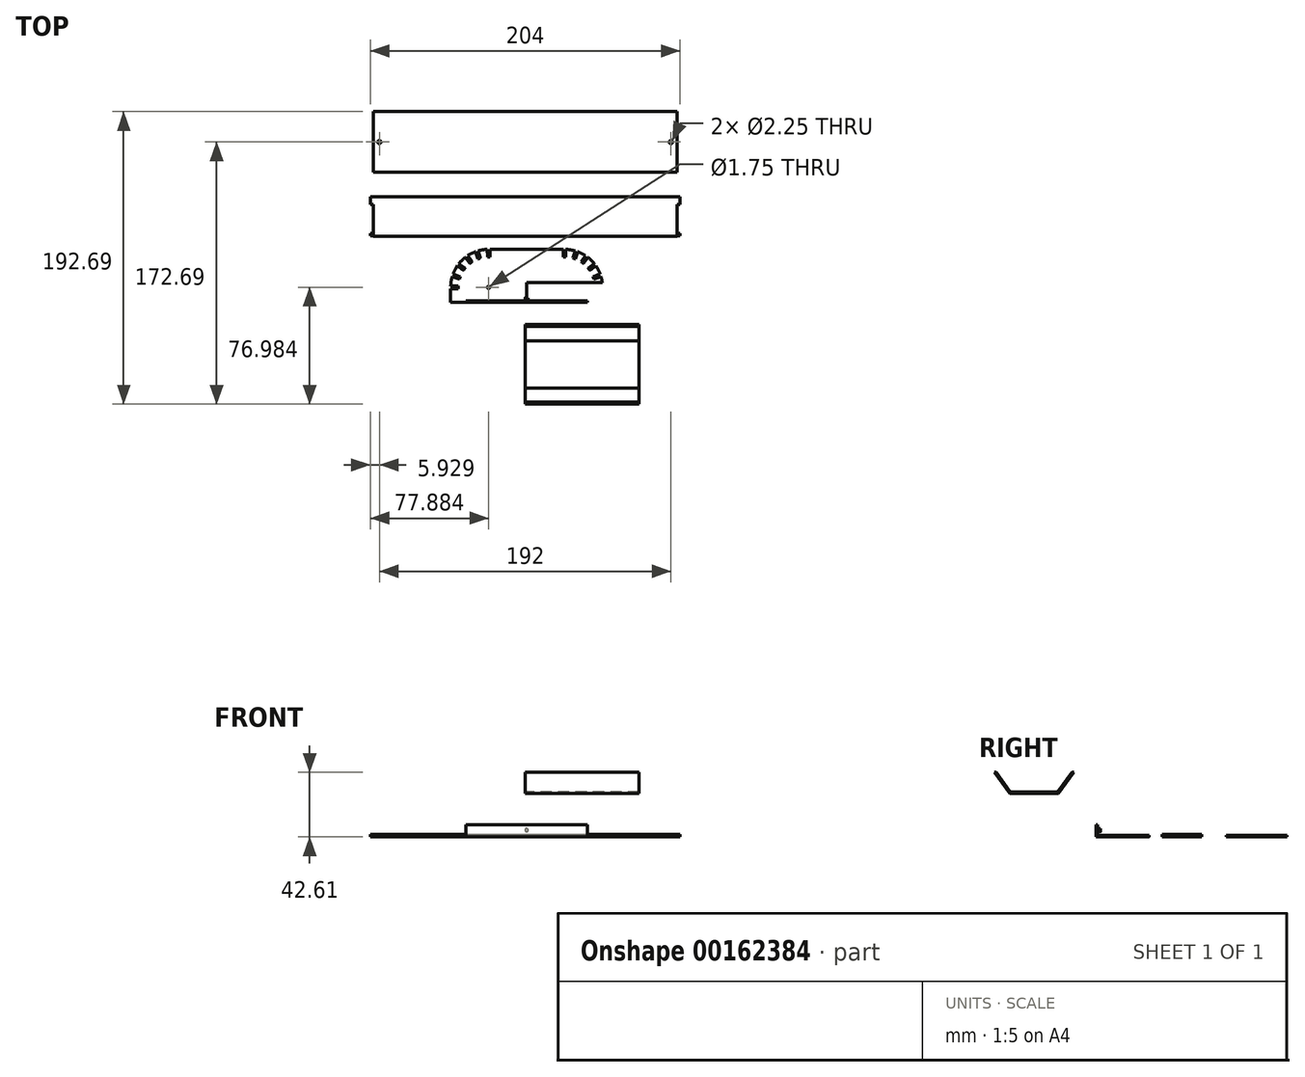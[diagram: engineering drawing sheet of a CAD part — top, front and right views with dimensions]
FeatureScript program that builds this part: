
annotation { "Feature Type Name" : "Feature", "Feature Type Description" : "" }
export const myFeature = defineFeature(function(context is Context, id is Id, definition is map)
    precondition{}
    {
        {
            var Q0;
            Q0=qCreatedBy(makeId("Top.planeOp"),FACE);
            var sketch = newSketch(context, id + "F0", { "sketchPlane" : qUnion([Q0])});
            skLineSegment(sketch, "E0.bottom", {"start": v(0, 0) * mm, "end": v(100, 0) * mm});
            skLineSegment(sketch, "E0.left", {"start": v(0, 0) * mm, "end": v(0, 26) * mm});
            skLineSegment(sketch, "E0.right", {"start": v(100, 0) * mm, "end": v(100, 21) * mm});
            skLineSegment(sketch, "E1", {"start": v(102, 26) * mm, "end": v(102, 21) * mm});
            skLineSegment(sketch, "E2", {"start": v(0, 26) * mm, "end": v(102, 26) * mm});
            skLineSegment(sketch, "E3", {"start": v(100, 21) * mm, "end": v(102, 21) * mm});
            skLineSegment(sketch, "E4.MirrorCS", {"start": v(-102, 26) * mm, "end": v(-102, 21) * mm});
            skLineSegment(sketch, "E5.MirrorCS", {"start": v(0, 26) * mm, "end": v(-102, 26) * mm});
            skLineSegment(sketch, "E6.MirrorCS", {"start": v(0, 0) * mm, "end": v(-100, 0) * mm});
            skLineSegment(sketch, "E7.MirrorCS", {"start": v(-100, 0) * mm, "end": v(-100, 21) * mm});
            skLineSegment(sketch, "E8.MirrorCS", {"start": v(-100, 21) * mm, "end": v(-102, 21) * mm});
            skPoint(sketch, "E9", {"position": v(0, 21) * mm});
            skPoint(sketch, "E10", {"position": v(0, 1) * mm});
            skSolve(sketch);
        }
        {
            var Q0;
            Q0=qCreatedBy(makeId("Top.planeOp"),FACE);
            var sketch = newSketch(context, id + "F1", { "sketchPlane" : qUnion([Q0])});
            skLineSegment(sketch, "E11", {"start": v(0.88, -33.7) * mm, "end": v(0.88, -8.7) * mm});
            skLineSegment(sketch, "E12", {"start": v(0.88, -8.7) * mm, "end": v(25, -8.7) * mm});
            skLineSegment(sketch, "E13", {"start": v(25.88, -30.7) * mm, "end": v(25.88, -30.87) * mm});
            skLineSegment(sketch, "E14", {"start": v(11.63, -33.7) * mm, "end": v(0.88, -33.7) * mm});
            skArc(sketch, "E15", {"start": v(26.76, -8.72) * mm, "mid": v(29.85, -9.02) * mm, "end": v(32.87, -9.7) * mm});
            skLineSegment(sketch, "E16.2", {"start": v(50.88, -43.7) * mm, "end": v(0.88, -43.7) * mm});
            skLineSegment(sketch, "E17.1", {"start": v(25.88, -30.7) * mm, "end": v(0.88, -30.7) * mm});
            skLineSegment(sketch, "E17.2", {"start": v(50.7, -30.7) * mm, "end": v(25.88, -30.7) * mm});
            skLineSegment(sketch, "E18", {"start": v(50.88, -34.58) * mm, "end": v(50.88, -43.7) * mm});
            skCircle(sketch, "E19", {"center": v(25.88, -33.7) * mm, "radius": 0.88 * mm});
            skLineSegment(sketch, "E20.0", {"start": v(45.14, -28.29) * mm, "end": v(49.87, -26.66) * mm});
            skLineSegment(sketch, "E21.0", {"start": v(31.3, -14.45) * mm, "end": v(32.87, -9.7) * mm});
            skArc(sketch, "E22.trimOffspring", {"start": v(34.53, -10.25) * mm, "mid": v(37.2, -11.42) * mm, "end": v(39.73, -12.89) * mm});
            skArc(sketch, "E23.trimOffspring", {"start": v(41.15, -13.9) * mm, "mid": v(43.45, -15.92) * mm, "end": v(45.48, -18.19) * mm});
            skArc(sketch, "E24.trimOffspring", {"start": v(46.52, -19.6) * mm, "mid": v(48.09, -22.21) * mm, "end": v(49.32, -25) * mm});
            skArc(sketch, "E25.trimOffspring", {"start": v(49.87, -26.66) * mm, "mid": v(50.56, -29.72) * mm, "end": v(50.87, -32.83) * mm});
            skLineSegment(sketch, "E26", {"start": v(0.88, -43.7) * mm, "end": v(0.88, -33.7) * mm});
            skLineSegment(sketch, "E27.MirrorCS", {"start": v(0.88, -43.7) * mm, "end": v(10.88, -43.7) * mm});
            skLineSegment(sketch, "E28.MirrorCS", {"start": v(26.68, -13.7) * mm, "end": v(24.93, -13.7) * mm});
            skLineSegment(sketch, "E29.MirrorCS", {"start": v(0.88, -30.7) * mm, "end": v(20.88, -30.7) * mm});
            skLineSegment(sketch, "E30.trimOffspring", {"start": v(24.93, -13.7) * mm, "end": v(25.88, -13.7) * mm});
            skArc(sketch, "E31.trimOffspring", {"start": v(31.3, -14.45) * mm, "mid": v(32.14, -14.7) * mm, "end": v(32.96, -15) * mm});
            skArc(sketch, "E32.trimOffspring", {"start": v(36.85, -16.98) * mm, "mid": v(37.57, -17.48) * mm, "end": v(38.27, -18) * mm});
            skArc(sketch, "E33.trimOffspring", {"start": v(41.48, -21.2) * mm, "mid": v(42.02, -21.89) * mm, "end": v(42.52, -22.6) * mm});
            skArc(sketch, "E34.trimOffspring", {"start": v(44.59, -26.62) * mm, "mid": v(44.88, -27.45) * mm, "end": v(45.14, -28.29) * mm});
            skLineSegment(sketch, "E35.trimOffspring", {"start": v(24.93, -13.7) * mm, "end": v(25, -8.7) * mm});
            skLineSegment(sketch, "E36.trimOffspring", {"start": v(26.68, -13.7) * mm, "end": v(26.76, -8.72) * mm});
            skPoint(sketch, "E37.start.orphan", {"position": v(25, -33.7) * mm});
            skLineSegment(sketch, "E38.trimOffspring", {"start": v(36.85, -16.98) * mm, "end": v(39.73, -12.89) * mm});
            skLineSegment(sketch, "E39.trimOffspring", {"start": v(38.27, -18) * mm, "end": v(41.15, -13.9) * mm});
            skLineSegment(sketch, "E40.trimOffspring", {"start": v(44.59, -26.62) * mm, "end": v(49.32, -25) * mm});
            skLineSegment(sketch, "E41.trimOffspring", {"start": v(42.52, -22.6) * mm, "end": v(46.52, -19.6) * mm});
            skLineSegment(sketch, "E42.trimOffspring", {"start": v(41.48, -21.2) * mm, "end": v(45.48, -18.19) * mm});
            skLineSegment(sketch, "E43.trimOffspring", {"start": v(32.96, -15) * mm, "end": v(34.53, -10.25) * mm});
            skPoint(sketch, "E44.start.orphan", {"position": v(26.76, -33.7) * mm});
            skLineSegment(sketch, "E45.MirrorCS", {"start": v(-9.87, -33.7) * mm, "end": v(0.88, -33.7) * mm});
            skLineSegment(sketch, "E46.0", {"start": v(50.88, -32.83) * mm, "end": v(45.88, -32.83) * mm});
            skLineSegment(sketch, "E47.0", {"start": v(50.88, -34.58) * mm, "end": v(45.88, -34.58) * mm});
            skLineSegment(sketch, "E48", {"start": v(45.88, -32.83) * mm, "end": v(45.88, -34.58) * mm});
            skPoint(sketch, "E49.MirrorCS.start.orphan", {"position": v(0.88, -8.7) * mm});
            skPoint(sketch, "E50.MirrorCS.end.orphan", {"position": v(0.88, -30.7) * mm});
            skLineSegment(sketch, "E51.MirrorCS", {"start": v(-24.91, -13.7) * mm, "end": v(-23.16, -13.7) * mm});
            skLineSegment(sketch, "E52.MirrorCS", {"start": v(-23.16, -13.7) * mm, "end": v(-24.12, -13.7) * mm});
            skLineSegment(sketch, "E53.MirrorCS", {"start": v(-24.12, -30.7) * mm, "end": v(-24.12, -30.87) * mm});
            skLineSegment(sketch, "E54.MirrorCS", {"start": v(0.88, -43.7) * mm, "end": v(-9.12, -43.7) * mm});
            skArc(sketch, "E55.MirrorCS", {"start": v(-35.09, -16.98) * mm, "mid": v(-35.8, -17.48) * mm, "end": v(-36.5, -18) * mm});
            skArc(sketch, "E56.MirrorCS", {"start": v(-42.82, -26.62) * mm, "mid": v(-43.11, -27.45) * mm, "end": v(-43.37, -28.29) * mm});
            skArc(sketch, "E57.MirrorCS", {"start": v(-39.72, -21.2) * mm, "mid": v(-40.25, -21.89) * mm, "end": v(-40.75, -22.6) * mm});
            skArc(sketch, "E58.MirrorCS", {"start": v(-29.54, -14.45) * mm, "mid": v(-30.37, -14.7) * mm, "end": v(-31.2, -15) * mm});
            skLineSegment(sketch, "E59.MirrorCS", {"start": v(-44.12, -32.83) * mm, "end": v(-44.12, -34.58) * mm});
            skCircle(sketch, "E60.MirrorC", {"center": v(-24.12, -33.7) * mm, "radius": 0.88 * mm});
            skLineSegment(sketch, "E61.MirrorCS", {"start": v(-24.91, -13.7) * mm, "end": v(-25, -8.72) * mm});
            skLineSegment(sketch, "E62.MirrorCS", {"start": v(-39.72, -21.2) * mm, "end": v(-43.72, -18.19) * mm});
            skLineSegment(sketch, "E63.MirrorCS", {"start": v(-43.37, -28.29) * mm, "end": v(-48.1, -26.66) * mm});
            skLineSegment(sketch, "E64.MirrorCS", {"start": v(-36.5, -18) * mm, "end": v(-39.38, -13.9) * mm});
            skPoint(sketch, "E65.MirrorP", {"position": v(-23.24, -33.7) * mm});
            skLineSegment(sketch, "E66.MirrorCS", {"start": v(-31.2, -15) * mm, "end": v(-32.77, -10.25) * mm});
            skLineSegment(sketch, "E67.MirrorCS", {"start": v(-48.94, -30.7) * mm, "end": v(-24.12, -30.7) * mm});
            skLineSegment(sketch, "E68.MirrorCS", {"start": v(-49.12, -34.58) * mm, "end": v(-44.12, -34.58) * mm});
            skLineSegment(sketch, "E69.MirrorCS", {"start": v(-35.09, -16.98) * mm, "end": v(-37.96, -12.89) * mm});
            skArc(sketch, "E70.MirrorCS", {"start": v(-25, -8.72) * mm, "mid": v(-28.08, -9.02) * mm, "end": v(-31.1, -9.7) * mm});
            skPoint(sketch, "E71.MirrorP", {"position": v(-25, -33.7) * mm});
            skLineSegment(sketch, "E72.MirrorCS", {"start": v(-23.24, -33.7) * mm, "end": v(0.88, -33.7) * mm});
            skArc(sketch, "E73.MirrorCS", {"start": v(-48.1, -26.66) * mm, "mid": v(-48.8, -29.72) * mm, "end": v(-49.1, -32.83) * mm});
            skLineSegment(sketch, "E74.MirrorCS", {"start": v(-23.16, -13.7) * mm, "end": v(-23.24, -8.7) * mm});
            skLineSegment(sketch, "E75.MirrorCS", {"start": v(0.88, -8.7) * mm, "end": v(-23.24, -8.7) * mm});
            skLineSegment(sketch, "E76.MirrorCS", {"start": v(-49.12, -34.58) * mm, "end": v(-49.12, -43.7) * mm});
            skLineSegment(sketch, "E77.MirrorCS", {"start": v(-29.54, -14.45) * mm, "end": v(-31.1, -9.7) * mm});
            skLineSegment(sketch, "E78.MirrorCS", {"start": v(0.88, -30.7) * mm, "end": v(-19.12, -30.7) * mm});
            skLineSegment(sketch, "E79.MirrorCS", {"start": v(-49.12, -43.7) * mm, "end": v(0.88, -43.7) * mm});
            skLineSegment(sketch, "E80.MirrorCS", {"start": v(-42.82, -26.62) * mm, "end": v(-47.55, -25) * mm});
            skArc(sketch, "E81.MirrorCS", {"start": v(-39.38, -13.9) * mm, "mid": v(-41.68, -15.92) * mm, "end": v(-43.72, -18.19) * mm});
            skArc(sketch, "E82.MirrorCS", {"start": v(-32.77, -10.25) * mm, "mid": v(-35.44, -11.42) * mm, "end": v(-37.96, -12.89) * mm});
            skLineSegment(sketch, "E83.MirrorCS", {"start": v(-24.12, -30.7) * mm, "end": v(0.88, -30.7) * mm});
            skLineSegment(sketch, "E84.MirrorCS", {"start": v(-49.12, -32.83) * mm, "end": v(-44.12, -32.83) * mm});
            skLineSegment(sketch, "E85.MirrorCS", {"start": v(-44.12, -33.7) * mm, "end": v(-25, -33.7) * mm});
            skLineSegment(sketch, "E86.MirrorCS", {"start": v(-40.75, -22.6) * mm, "end": v(-44.75, -19.6) * mm});
            skArc(sketch, "E87.MirrorCS", {"start": v(-44.75, -19.6) * mm, "mid": v(-46.32, -22.21) * mm, "end": v(-47.55, -25) * mm});
            skPoint(sketch, "E88.start.orphan", {"position": v(45.88, -33.7) * mm});
            skPoint(sketch, "E89.MirrorCS.end.orphan", {"position": v(0.88, -33.7) * mm});
            skPoint(sketch, "E89.MirrorCS.start.orphan", {"position": v(11.63, -33.7) * mm});
            skLineSegment(sketch, "E90.bottom", {"start": v(0.88, -42.7) * mm, "end": v(40.88, -42.7) * mm});
            skLineSegment(sketch, "E90.top", {"start": v(5.88, -43.7) * mm, "end": v(40.88, -43.7) * mm});
            skLineSegment(sketch, "E90.right", {"start": v(40.88, -42.7) * mm, "end": v(40.88, -43.7) * mm});
            skLineSegment(sketch, "E91.MirrorCS", {"start": v(0.88, -42.7) * mm, "end": v(-39.12, -42.7) * mm});
            skLineSegment(sketch, "E92.MirrorCS", {"start": v(-39.12, -42.7) * mm, "end": v(-39.12, -43.7) * mm});
            skSolve(sketch);
        }
        {
            var Q0;
            Q0=makeQuery(id+"F1.imprint","IMPRINT",FACE,{"disambiguationData":[TD([[makeQuery(id+"F1.imprint","IMPRINT",EDGE,{"derivedFrom":sQuery(id+"F1.wireOp",EDGE,"E16.2")}),-1.0]])]});
            var Q1;
            {var subQ10=sQuery(id+"F1.wireOp",EDGE,"E67.MirrorCS");Q1=makeQuery(id+"F1.imprint","IMPRINT",FACE,{"disambiguationData":[TD([[makeQuery(id+"F1.imprint","IMPRINT",EDGE,{"derivedFrom":subQ10}),-1.0]])]});}
            var Q2;
            {var subQ4=sQuery(id+"F1.wireOp",EDGE,"E68.MirrorCS");Q2=makeQuery(id+"F1.imprint","IMPRINT",FACE,{"disambiguationData":[TD([[makeQuery(id+"F1.imprint","IMPRINT",EDGE,{"derivedFrom":subQ4}),-1.0]])]});}
            var Q3;
            Q3=makeQuery(id+"F1.imprint","IMPRINT",FACE,{"disambiguationData":[TD([[makeQuery(id+"F1.imprint","IMPRINT",EDGE,{"derivedFrom":sQuery(id+"F1.wireOp",EDGE,"E51.MirrorCS")}),-1.0]])]});
            var Q4;
            {var subQ4=sQuery(id+"F1.wireOp",EDGE,"E12");Q4=makeQuery(id+"F1.imprint","IMPRINT",FACE,{"disambiguationData":[TD([[makeQuery(id+"F1.imprint","IMPRINT",EDGE,{"derivedFrom":subQ4}),-1.0]])]});}
            var Q5;
            {var subQ5=sQuery(id+"F1.wireOp",EDGE,"E91.MirrorCS");Q5=makeQuery(id+"F1.imprint","IMPRINT",FACE,{"disambiguationData":[TD([[makeQuery(id+"F1.imprint","IMPRINT",EDGE,{"derivedFrom":subQ5}),1.0]])]});}
            var Q6;
            {var subQ3=sQuery(id+"F1.wireOp",EDGE,"E90.bottom");Q6=makeQuery(id+"F1.imprint","IMPRINT",FACE,{"disambiguationData":[TD([[makeQuery(id+"F1.imprint","IMPRINT",EDGE,{"derivedFrom":subQ3}),-1.0]])]});}
            extrude(context, id + "F2", {"entities" : qUnion([Q0, Q1, Q2, Q3, Q4, Q5, Q6]), "depth" : 1 * mm});
        }
        {
            var Q0;
            Q0=makeQuery(id+"F0.imprint","IMPRINT",FACE,{"disambiguationData":[TD([[makeQuery(id+"F0.imprint","IMPRINT",EDGE,{"derivedFrom":sQuery(id+"F0.wireOp",EDGE,"E0.bottom")}),1.0]])]});
            var Q1;
            Q1=makeQuery(id+"F0.imprint","IMPRINT",FACE,{"disambiguationData":[TD([[makeQuery(id+"F0.imprint","IMPRINT",EDGE,{"derivedFrom":sQuery(id+"F0.wireOp",EDGE,"E0.left")}),1.0]])]});
            extrude(context, id + "F3", {"entities" : qUnion([Q0, Q1]), "depth" : 1.75 * mm});
        }
        {
            var Q0;
            {var subQ5=sQuery(id+"F1.wireOp",EDGE,"E91.MirrorCS");Q0=makeQuery(id+"F1.imprint","IMPRINT",FACE,{"disambiguationData":[TD([[makeQuery(id+"F1.imprint","IMPRINT",EDGE,{"derivedFrom":subQ5}),1.0]])]});}
            var Q1;
            {var subQ3=sQuery(id+"F1.wireOp",EDGE,"E90.bottom");Q1=makeQuery(id+"F1.imprint","IMPRINT",FACE,{"disambiguationData":[TD([[makeQuery(id+"F1.imprint","IMPRINT",EDGE,{"derivedFrom":subQ3}),-1.0]])]});}
            extrude(context, id + "F4", {"entities" : qUnion([Q0, Q1]), "operationType" : NewBodyOperationType.ADD, "depth" : 8 * mm});
        }
        {
            var Q0;
            Q0=makeQuery(id+"F4.opExtrude","SWEPT_FACE",FACE,{"disambiguationData":[OSD([sQuery(id+"F1.wireOp",EDGE,"E90.bottom"),sQuery(id+"F1.wireOp",EDGE,"E91.MirrorCS")])]});
            var sketch = newSketch(context, id + "F5", { "sketchPlane" : qUnion([Q0])});
            skPoint(sketch, "E93", {"position": v(-0.88, 8) * mm});
            skPoint(sketch, "E94", {"position": v(-0.88, 4.5) * mm});
            skCircle(sketch, "E95", {"center": v(-0.88, 4.5) * mm, "radius": 1 * mm});
            skLineSegment(sketch, "E96", {"start": v(-40.88, 4.5) * mm, "end": v(39.12, 4.5) * mm, "construction": true});
            skSolve(sketch);
        }
        {
            var Q0;
            Q0 = qSketchRegion(id + "F5", true);
            extrude(context, id + "F6", {"entities" : qUnion([Q0]), "operationType" : NewBodyOperationType.ADD, "depth" : 2 * mm});
        }
        {
            var Q0;
            Q0=qCreatedBy(makeId("Top.planeOp"),FACE);
            var sketch = newSketch(context, id + "F7", { "sketchPlane" : qUnion([Q0])});
            skLineSegment(sketch, "E97.bottom", {"start": v(99.93, 42) * mm, "end": v(99.93, 82) * mm});
            skLineSegment(sketch, "E97.top", {"start": v(-100.07, 42) * mm, "end": v(-100.07, 82) * mm});
            skLineSegment(sketch, "E97.left", {"start": v(99.93, 42) * mm, "end": v(-100.07, 42) * mm});
            skLineSegment(sketch, "E97.right", {"start": v(99.93, 82) * mm, "end": v(-100.07, 82) * mm});
            skCircle(sketch, "E98", {"center": v(95.93, 62) * mm, "radius": 1.13 * mm});
            skPoint(sketch, "E98.centerSnap0", {"position": v(99.93, 62) * mm});
            skLineSegment(sketch, "E99", {"start": v(-0.07, 42) * mm, "end": v(-0.07, 82) * mm, "construction": true});
            skCircle(sketch, "E100.MirrorC", {"center": v(-96.07, 62) * mm, "radius": 1.13 * mm});
            skSolve(sketch);
        }
        {
            var Q0;
            Q0=makeQuery(id+"F7.imprint","IMPRINT",FACE,{"disambiguationData":[TD([[makeQuery(id+"F7.imprint","IMPRINT",EDGE,{"derivedFrom":sQuery(id+"F7.wireOp",EDGE,"E97.bottom")}),1.0]])]});
            extrude(context, id + "F8", {"entities" : qUnion([Q0]), "depth" : 1 * mm});
        }
        {
            var Q0;
            Q0=makeQuery(id+"F3.opExtrude","SWEPT_FACE",FACE,{"disambiguationData":[OSD([sQuery(id+"F0.wireOp",EDGE,"E7.MirrorCS")])]});
            var sketch = newSketch(context, id + "F9", { "sketchPlane" : qUnion([Q0])});
            skLineSegment(sketch, "E101", {"start": v(-1, 0) * mm, "end": v(-1, 1.75) * mm});
            skCircle(sketch, "E102", {"center": v(-1, 0.88) * mm, "radius": 0.75 * mm});
            skSolve(sketch);
        }
        {
            var Q0;
            {var subQ0=sQuery(id+"F9.wireOp",EDGE,"E102");var subQ1=sQuery(id+"F9.wireOp",EDGE,"E101");var subQ2=makeQuery(id+"F9.imprint","INTERSECT",VERTEX,{"disambiguationData":[OD(0.0)],"derivedFrom":[subQ1,subQ0]});Q0=makeQuery(id+"F9.imprint","IMPRINT",FACE,{"disambiguationData":[TD([[makeQuery(id+"F9.imprint","IMPRINT",EDGE,{"disambiguationData":[TD([[subQ2,-1.0]])],"derivedFrom":subQ1}),1.0]])]});}
            var Q1;
            {var subQ0=sQuery(id+"F9.wireOp",EDGE,"E102");var subQ1=sQuery(id+"F9.wireOp",EDGE,"E101");var subQ2=makeQuery(id+"F9.imprint","INTERSECT",VERTEX,{"disambiguationData":[OD(0.0)],"derivedFrom":[subQ1,subQ0]});Q1=makeQuery(id+"F9.imprint","IMPRINT",FACE,{"disambiguationData":[TD([[makeQuery(id+"F9.imprint","IMPRINT",EDGE,{"disambiguationData":[TD([[subQ2,-1.0]])],"derivedFrom":subQ1}),-1.0]])]});}
            var Q2;
            Q2=sQuery(id+"F9.wireOp",EDGE,"E102");
            extrude(context, id + "F10", {"entities" : qUnion([Q0, Q1]), "operationType" : NewBodyOperationType.ADD, "surfaceEntities" : qUnion([Q2]), "depth" : 2 * mm});
        }
        {
            var Q0;
            {var subQ0=sQuery(id+"F9.wireOp",EDGE,"E102");var subQ1=sQuery(id+"F9.wireOp",EDGE,"E101");var subQ2=makeQuery(id+"F9.imprint","INTERSECT",VERTEX,{"disambiguationData":[OD(0.0)],"derivedFrom":[subQ1,subQ0]});Q0=makeQuery(id+"F9.imprint","IMPRINT",FACE,{"disambiguationData":[TD([[makeQuery(id+"F9.imprint","IMPRINT",EDGE,{"disambiguationData":[TD([[subQ2,-1.0]])],"derivedFrom":subQ1}),1.0]])]});}
            var Q1;
            {var subQ0=sQuery(id+"F9.wireOp",EDGE,"E102");var subQ1=sQuery(id+"F9.wireOp",EDGE,"E101");var subQ2=makeQuery(id+"F9.imprint","INTERSECT",VERTEX,{"disambiguationData":[OD(0.0)],"derivedFrom":[subQ1,subQ0]});Q1=makeQuery(id+"F9.imprint","IMPRINT",FACE,{"disambiguationData":[TD([[makeQuery(id+"F9.imprint","IMPRINT",EDGE,{"disambiguationData":[TD([[subQ2,-1.0]])],"derivedFrom":subQ1}),-1.0]])]});}
            extrude(context, id + "F11", {"entities" : qUnion([Q0, Q1]), "operationType" : NewBodyOperationType.ADD, "oppositeDirection" : true, "depth" : 202 * mm});
        }
        {
            var Q0;
            Q0=qCreatedBy(makeId("Right.planeOp"),FACE);
            var sketch = newSketch(context, id + "F12", { "sketchPlane" : qUnion([Q0])});
            skLineSegment(sketch, "E103", {"start": v(-84.51, 28.6) * mm, "end": v(-100.51, 28.6) * mm});
            skLineSegment(sketch, "E104", {"start": v(-100.51, 28.6) * mm, "end": v(-110.7, 42.61) * mm});
            skLineSegment(sketch, "E105", {"start": v(-110.7, 42.61) * mm, "end": v(-109.45, 42.61) * mm});
            skLineSegment(sketch, "E106", {"start": v(-84.51, 42.61) * mm, "end": v(-84.51, 28.6) * mm, "construction": true});
            skLineSegment(sketch, "E107.0", {"start": v(-100, 29.6) * mm, "end": v(-109.45, 42.61) * mm});
            skLineSegment(sketch, "E107.1", {"start": v(-84.51, 29.6) * mm, "end": v(-100, 29.6) * mm});
            skLineSegment(sketch, "E108.MirrorCS", {"start": v(-58.33, 42.61) * mm, "end": v(-59.57, 42.61) * mm});
            skLineSegment(sketch, "E109.MirrorCS", {"start": v(-84.51, 29.6) * mm, "end": v(-69.02, 29.6) * mm});
            skLineSegment(sketch, "E110.MirrorCS", {"start": v(-68.51, 28.6) * mm, "end": v(-58.33, 42.61) * mm});
            skLineSegment(sketch, "E111.MirrorCS", {"start": v(-69.02, 29.6) * mm, "end": v(-59.57, 42.61) * mm});
            skLineSegment(sketch, "E112.MirrorCS", {"start": v(-84.51, 28.6) * mm, "end": v(-68.51, 28.6) * mm});
            skSolve(sketch);
        }
        {
            var Q0;
            Q0 = qSketchRegion(id + "F12", true);
            extrude(context, id + "F13", {"entities" : qUnion([Q0]), "operationType" : NewBodyOperationType.ADD, "depth" : 75 * mm});
        }
    });
